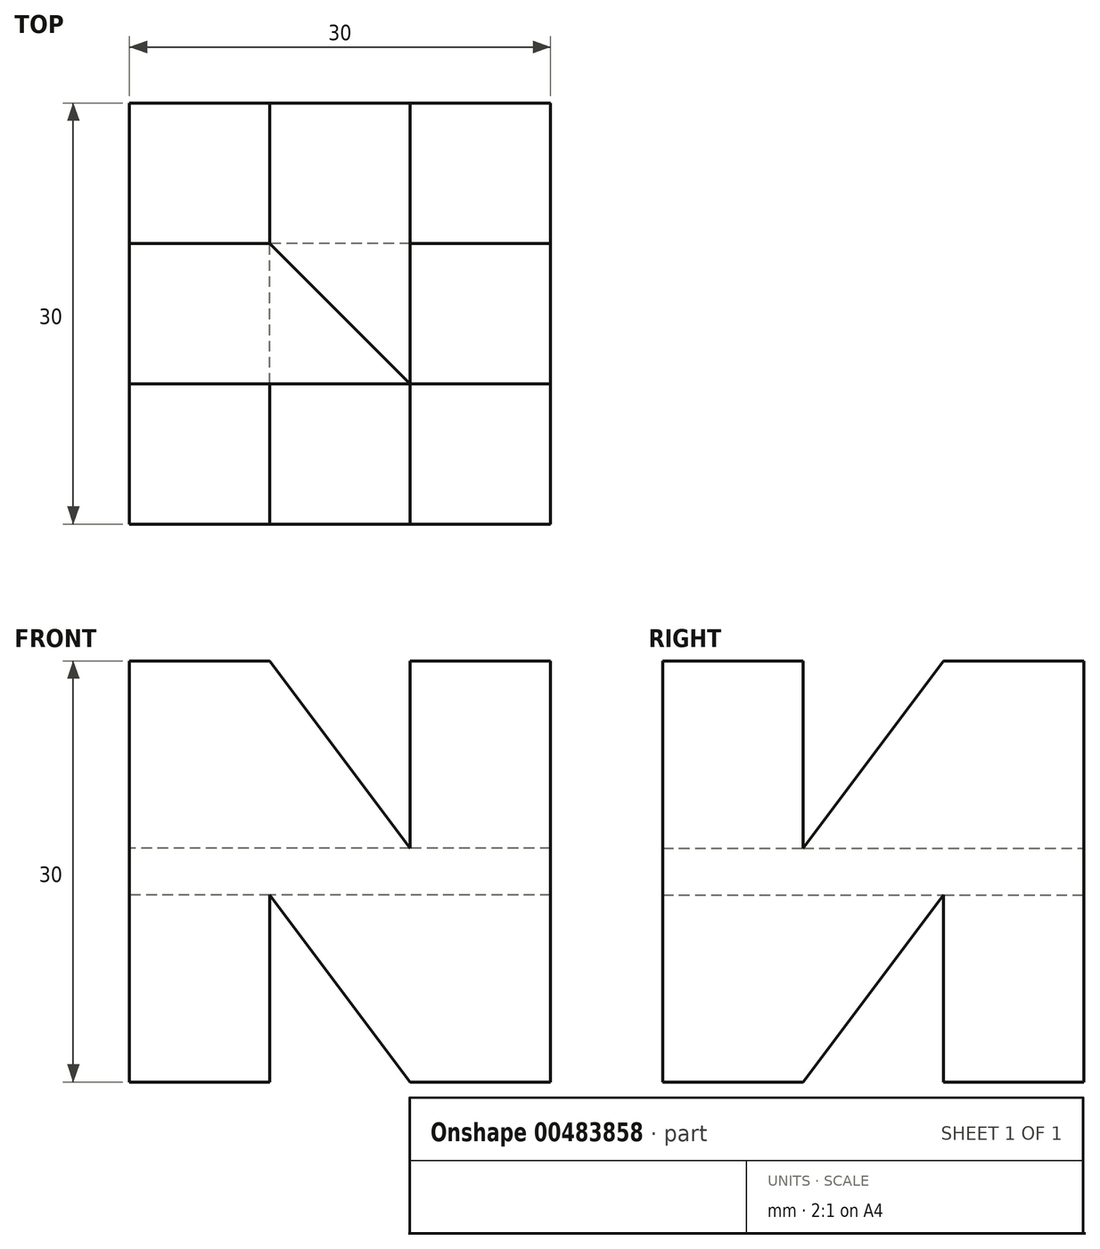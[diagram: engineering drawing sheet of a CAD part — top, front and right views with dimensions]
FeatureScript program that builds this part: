
annotation { "Feature Type Name" : "Feature", "Feature Type Description" : "" }
export const myFeature = defineFeature(function(context is Context, id is Id, definition is map)
    precondition{}
    {
        {
            var Q0;
            Q0=qCreatedBy(makeId("Front.planeOp"),FACE);
            var sketch = newSketch(context, id + "F0", { "sketchPlane" : qUnion([Q0])});
            skLineSegment(sketch, "E0", {"start": v(-30, 0) * mm, "end": v(-30, 30) * mm});
            skLineSegment(sketch, "E1", {"start": v(-30, 30) * mm, "end": v(-20, 30) * mm});
            skLineSegment(sketch, "E2", {"start": v(-20, 30) * mm, "end": v(-10, 16.67) * mm});
            skLineSegment(sketch, "E3", {"start": v(-10, 16.67) * mm, "end": v(-10, 30) * mm});
            skLineSegment(sketch, "E4", {"start": v(-10, 30) * mm, "end": v(0, 30) * mm});
            skLineSegment(sketch, "E5", {"start": v(0, 30) * mm, "end": v(0, 0) * mm});
            skLineSegment(sketch, "E6", {"start": v(0, 0) * mm, "end": v(-10, 0) * mm});
            skLineSegment(sketch, "E7", {"start": v(-10, 0) * mm, "end": v(-20, 13.33) * mm});
            skLineSegment(sketch, "E8", {"start": v(-20, 13.33) * mm, "end": v(-20, 0) * mm});
            skLineSegment(sketch, "E9", {"start": v(-20, 0) * mm, "end": v(-30, 0) * mm});
            skSolve(sketch);
        }
        {
            var Q0;
            Q0=makeQuery(id+"F0.imprint","IMPRINT",FACE,{"disambiguationData":[TD([[makeQuery(id+"F0.imprint","IMPRINT",EDGE,{"derivedFrom":sQuery(id+"F0.wireOp",EDGE,"E0")}),-1.0]])]});
            extrude(context, id + "F1", {"entities" : qUnion([Q0]), "depth" : 30 * mm});
        }
        {
            var Q0;
            Q0=makeQuery(id+"F1.opExtrude","SWEPT_FACE",FACE,{"disambiguationData":[OSD([sQuery(id+"F0.wireOp",EDGE,"E0")])]});
            var sketch = newSketch(context, id + "F2", { "sketchPlane" : qUnion([Q0])});
            skLineSegment(sketch, "E10", {"start": v(10, 0) * mm, "end": v(10, 13.33) * mm});
            skLineSegment(sketch, "E11", {"start": v(10, 13.33) * mm, "end": v(20, 0) * mm});
            skLineSegment(sketch, "E12", {"start": v(10, 0) * mm, "end": v(20, 0) * mm});
            skLineSegment(sketch, "E13", {"start": v(10, 30) * mm, "end": v(20, 30) * mm});
            skLineSegment(sketch, "E14", {"start": v(20, 30) * mm, "end": v(20, 16.67) * mm});
            skLineSegment(sketch, "E15", {"start": v(20, 16.67) * mm, "end": v(10, 30) * mm});
            skSolve(sketch);
        }
        {
            var Q0;
            Q0=makeQuery(id+"F2.imprint","IMPRINT",FACE,{"disambiguationData":[TD([[makeQuery(id+"F2.imprint","IMPRINT",EDGE,{"derivedFrom":sQuery(id+"F2.wireOp",EDGE,"E13")}),1.0]])]});
            var Q1;
            Q1=makeQuery(id+"F2.imprint","IMPRINT",FACE,{"disambiguationData":[TD([[makeQuery(id+"F2.imprint","IMPRINT",EDGE,{"derivedFrom":sQuery(id+"F2.wireOp",EDGE,"E10")}),-1.0]])]});
            extrude(context, id + "F3", {"entities" : qUnion([Q0, Q1]), "operationType" : NewBodyOperationType.REMOVE, "endBound" : BoundingType.THROUGH_ALL, "oppositeDirection" : true, "depth" : 25 * mm});
        }
    });
